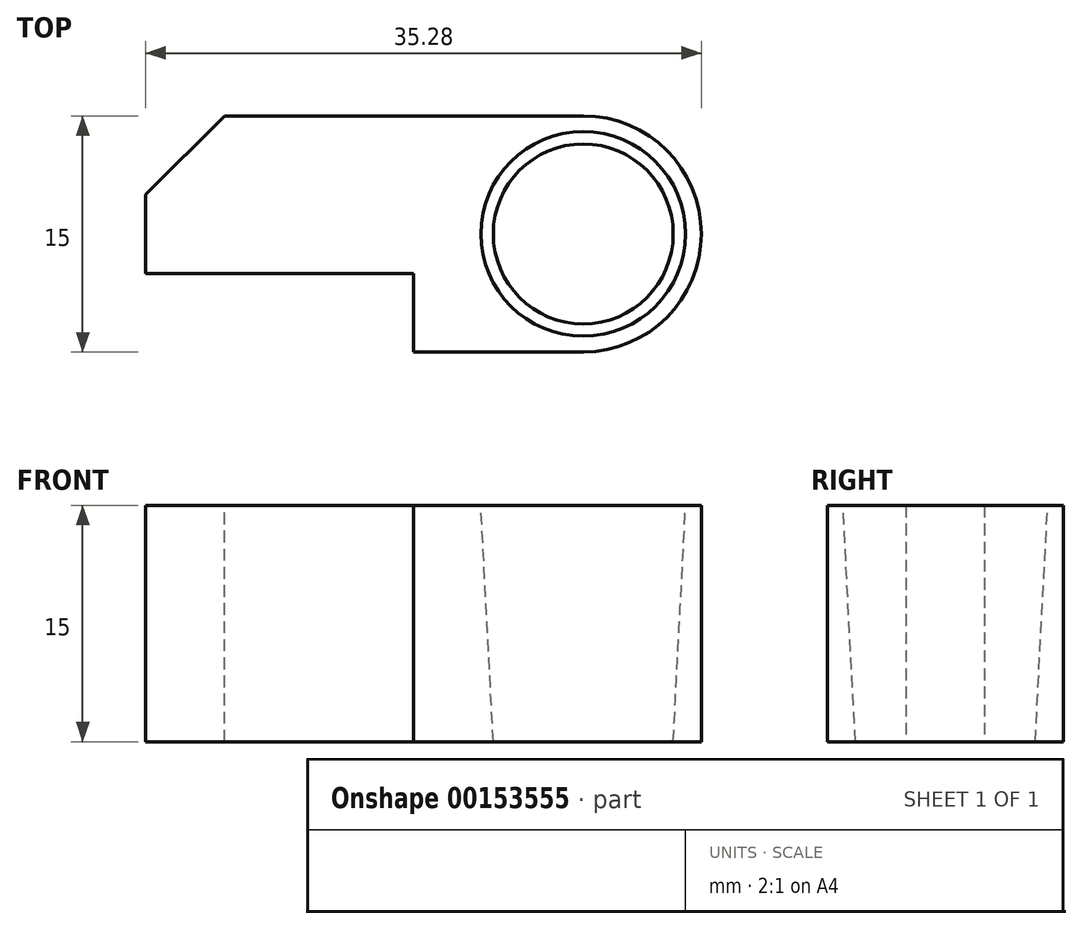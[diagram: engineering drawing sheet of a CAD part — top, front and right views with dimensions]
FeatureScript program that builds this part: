
annotation { "Feature Type Name" : "Feature", "Feature Type Description" : "" }
export const myFeature = defineFeature(function(context is Context, id is Id, definition is map)
    precondition{}
    {
        {
            var Q0;
            Q0=qCreatedBy(makeId("Top.planeOp"),FACE);
            var sketch = newSketch(context, id + "F0", { "sketchPlane" : qUnion([Q0])});
            skLineSegment(sketch, "E0.bottom", {"start": v(7, -5) * mm, "end": v(-10, -5) * mm});
            skLineSegment(sketch, "E0.top", {"start": v(10, 5) * mm, "end": v(-10, 5) * mm});
            skLineSegment(sketch, "E0.right", {"start": v(-10, -5) * mm, "end": v(-10, 5) * mm});
            skPoint(sketch, "E0.middle", {"position": v(0, 0) * mm});
            skLineSegment(sketch, "E1.top", {"start": v(10, -10) * mm, "end": v(7, -10) * mm});
            skLineSegment(sketch, "E1.right", {"start": v(7, -5) * mm, "end": v(7, -10) * mm});
            skLineSegment(sketch, "E2", {"start": v(10, 5) * mm, "end": v(29.85, 5) * mm, "construction": true});
            skArc(sketch, "E3", {"start": v(17.78, -10) * mm, "mid": v(25.28, -2.5) * mm, "end": v(17.78, 5) * mm});
            skLineSegment(sketch, "E4", {"start": v(10, -10) * mm, "end": v(17.78, -10) * mm});
            skLineSegment(sketch, "E5", {"start": v(17.78, 5) * mm, "end": v(10, 5) * mm});
            skSolve(sketch);
        }
        {
            var Q0;
            Q0 = qSketchRegion(id + "F0", true);
            extrude(context, id + "F1", {"entities" : qUnion([Q0]), "depth" : 15 * mm});
        }
        {
            var Q0;
            Q0=makeQuery(id+"F1.opExtrude","CAP_FACE",FACE,{"disambiguationData":[OSD([sQuery(id+"F0.wireOp",EDGE,"E0.bottom"),sQuery(id+"F0.wireOp",EDGE,"E0.top"),sQuery(id+"F0.wireOp",EDGE,"E0.right"),sQuery(id+"F0.wireOp",EDGE,"E1.top"),sQuery(id+"F0.wireOp",EDGE,"E1.right"),sQuery(id+"F0.wireOp",EDGE,"E3"),sQuery(id+"F0.wireOp",EDGE,"E4"),sQuery(id+"F0.wireOp",EDGE,"E5")])],"isStart":false});
            var sketch = newSketch(context, id + "F2", { "sketchPlane" : qUnion([Q0])});
            skCircle(sketch, "E6", {"center": v(17.78, -2.5) * mm, "radius": 6.5 * mm});
            skSolve(sketch);
        }
        {
            var Q0;
            Q0 = qSketchRegion(id + "F2", true);
            var Q1;
            Q1=makeQuery(id+"F1.opExtrude","CAP_FACE",FACE,{"disambiguationData":[OSD([sQuery(id+"F0.wireOp",EDGE,"E0.bottom"),sQuery(id+"F0.wireOp",EDGE,"E0.top"),sQuery(id+"F0.wireOp",EDGE,"E0.right"),sQuery(id+"F0.wireOp",EDGE,"E1.top"),sQuery(id+"F0.wireOp",EDGE,"E1.right"),sQuery(id+"F0.wireOp",EDGE,"E3"),sQuery(id+"F0.wireOp",EDGE,"E4"),sQuery(id+"F0.wireOp",EDGE,"E5")])],"isStart":true});
            extrude(context, id + "F3", {"entities" : qUnion([Q0]), "operationType" : NewBodyOperationType.REMOVE, "endBound" : BoundingType.UP_TO_SURFACE, "oppositeDirection" : true, "endBoundEntityFace" : qUnion([Q1]), "depth" : 25 * mm, "hasDraft" : true, "draftAngle" : 3 * degree, "draftPullDirection" : true});
        }
        {
            var Q0;
            Q0=makeQuery(id+"F1.opExtrude","SWEPT_EDGE",EDGE,{"disambiguationData":[OSD([sQuery(id+"F0.wireOp",EDGE,"E0.top"),sQuery(id+"F0.wireOp",EDGE,"E0.right")])]});
            chamfer(context, id + "F4", {"entities" : qUnion([Q0]), "width" : 5 * mm, "tangentPropagation" : true});
        }
    });
